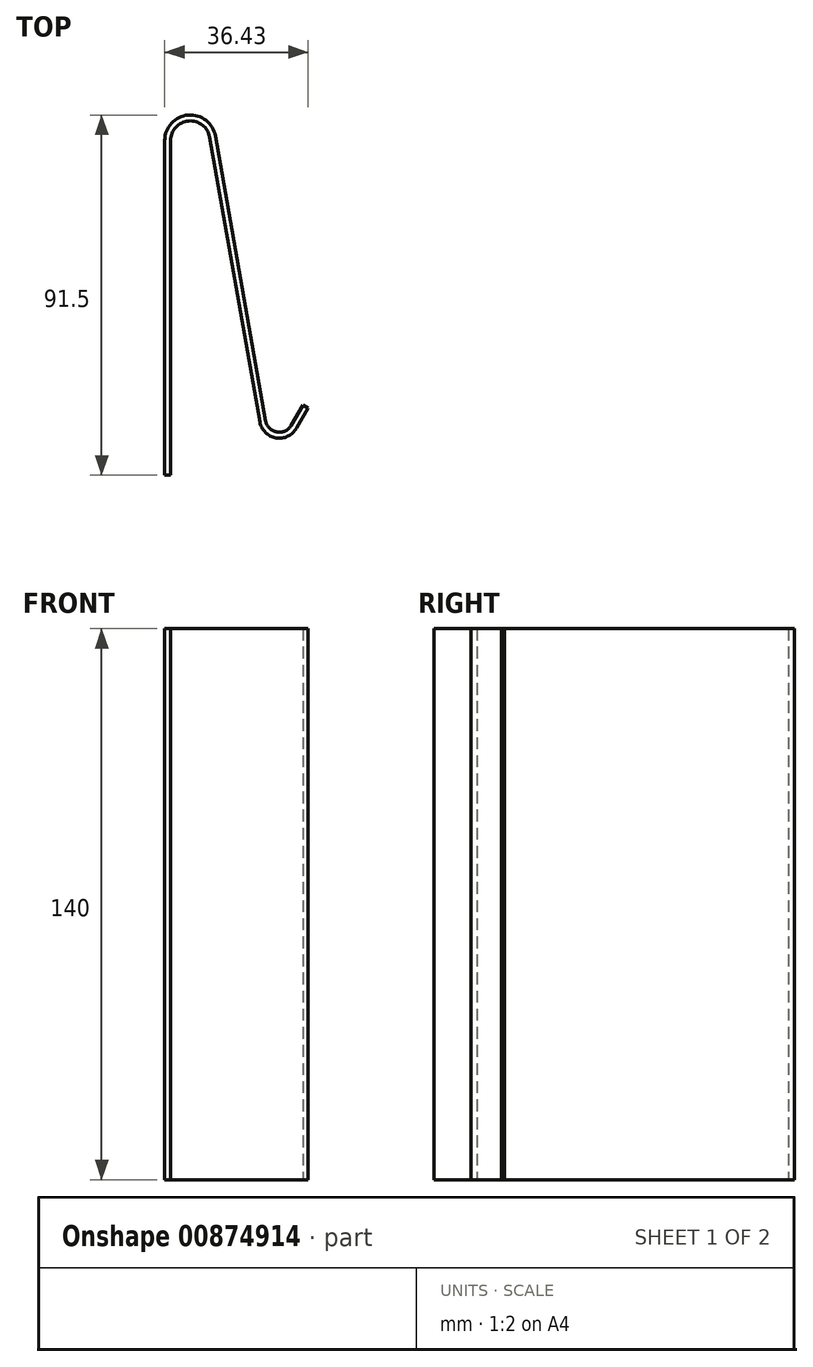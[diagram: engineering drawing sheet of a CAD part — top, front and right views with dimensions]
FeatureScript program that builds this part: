
annotation { "Feature Type Name" : "Feature", "Feature Type Description" : "" }
export const myFeature = defineFeature(function(context is Context, id is Id, definition is map)
    precondition{}
    {
        {
            var Q0;
            Q0=qCreatedBy(makeId("Top.planeOp"),FACE);
            var sketch = newSketch(context, id + "F0", { "sketchPlane" : qUnion([Q0])});
            skLineSegment(sketch, "E0", {"start": v(0, 0) * mm, "end": v(0, 85) * mm});
            skLineSegment(sketch, "E1", {"start": v(9.92, 85.87) * mm, "end": v(22.68, 13.53) * mm});
            skLineSegment(sketch, "E2", {"start": v(31.93, 11.9) * mm, "end": v(34.93, 17.1) * mm});
            skPoint(sketch, "E3.visualSharp", {"position": v(0, 142.15) * mm});
            skArc(sketch, "E3.filletArc", {"start": v(9.92, 85.87) * mm, "mid": v(4.56, 89.98) * mm, "end": v(0, 85) * mm});
            skPoint(sketch, "E4.visualSharp", {"position": v(25.06, 0) * mm});
            skArc(sketch, "E4.filletArc", {"start": v(22.68, 13.53) * mm, "mid": v(26.74, 9.47) * mm, "end": v(31.93, 11.9) * mm});
            skLineSegment(sketch, "E5.0", {"start": v(30.63, 12.65) * mm, "end": v(33.63, 17.84) * mm});
            skLineSegment(sketch, "E5.1", {"start": v(-1.5, 0) * mm, "end": v(-1.5, 85) * mm});
            skArc(sketch, "E5.2", {"start": v(11.4, 86.13) * mm, "mid": v(4.43, 91.48) * mm, "end": v(-1.5, 85) * mm});
            skLineSegment(sketch, "E5.3", {"start": v(11.4, 86.13) * mm, "end": v(24.16, 13.79) * mm});
            skArc(sketch, "E5.4", {"start": v(24.16, 13.79) * mm, "mid": v(27, 10.95) * mm, "end": v(30.63, 12.65) * mm});
            skLineSegment(sketch, "E6", {"start": v(-1.5, 0) * mm, "end": v(0, 0) * mm});
            skLineSegment(sketch, "E7", {"start": v(33.63, 17.84) * mm, "end": v(34.93, 17.1) * mm});
            skSolve(sketch);
        }
        {
            var Q0;
            Q0=makeQuery(id+"F0.imprint","IMPRINT",FACE,{"disambiguationData":[TD([[makeQuery(id+"F0.imprint","IMPRINT",EDGE,{"derivedFrom":sQuery(id+"F0.wireOp",EDGE,"E0")}),1.0]])]});
            extrude(context, id + "F1", {"entities" : qUnion([Q0]), "depth" : 140 * mm, "offsetDistance" : 25 * mm});
        }
    });
